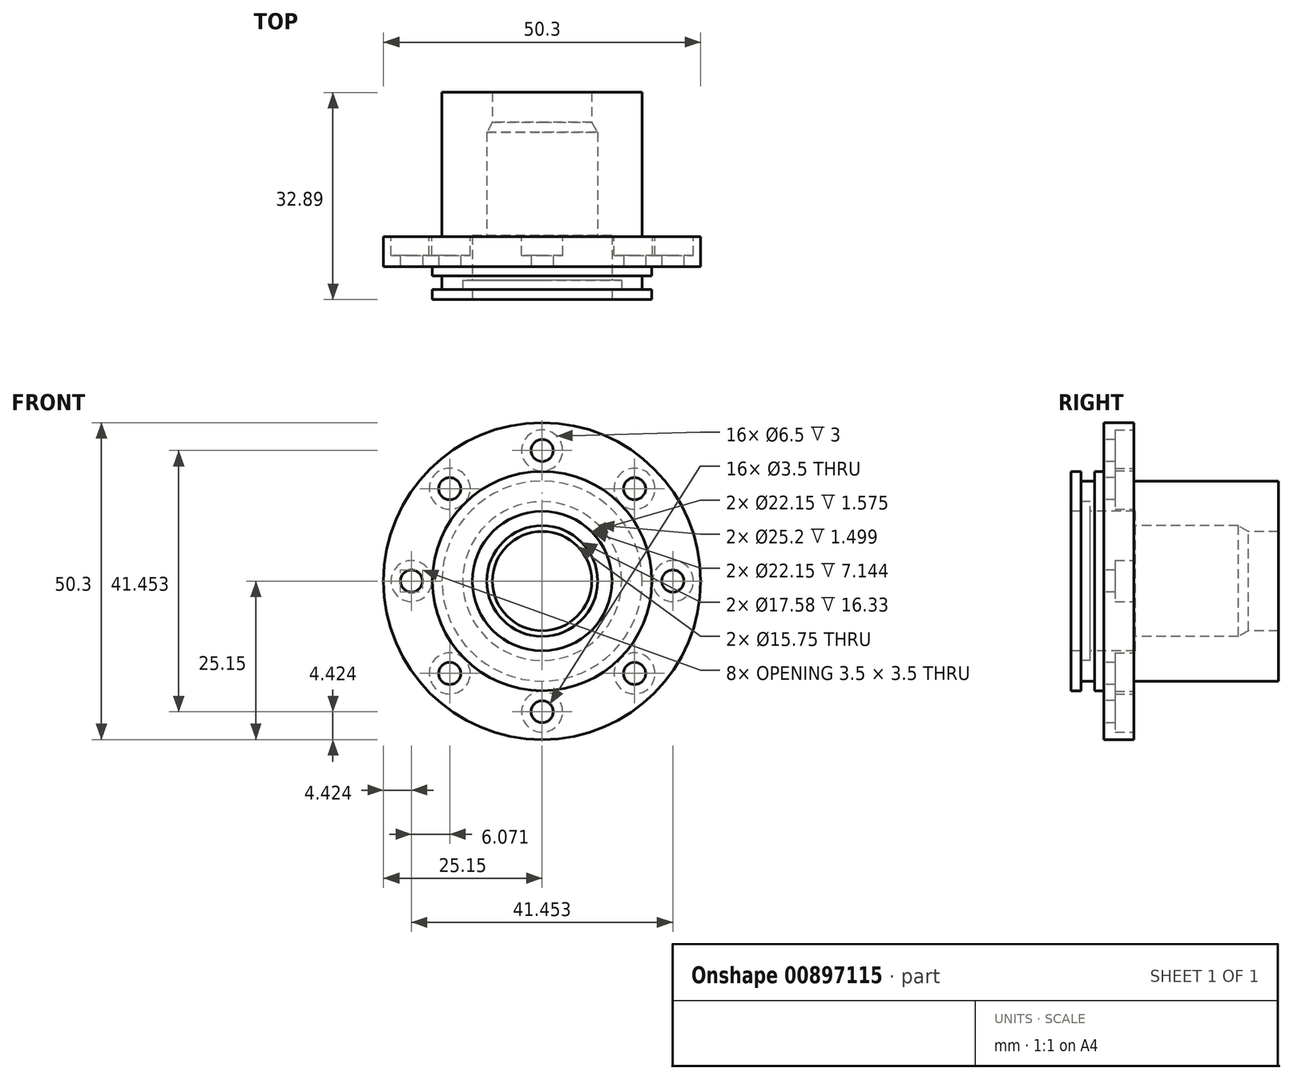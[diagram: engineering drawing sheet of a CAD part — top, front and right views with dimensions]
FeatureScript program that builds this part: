
annotation { "Feature Type Name" : "Feature", "Feature Type Description" : "" }
export const myFeature = defineFeature(function(context is Context, id is Id, definition is map)
    precondition{}
    {
        {
            var Q0;
            Q0=qCreatedBy(makeId("Right.planeOp"),FACE);
            var sketch = newSketch(context, id + "F0", { "sketchPlane" : qUnion([Q0])});
            skLineSegment(sketch, "E0", {"start": v(0, 17.4) * mm, "end": v(1.63, 17.4) * mm});
            skLineSegment(sketch, "E1", {"start": v(1.63, 17.4) * mm, "end": v(1.63, 15.88) * mm});
            skLineSegment(sketch, "E2", {"start": v(5.23, 25.15) * mm, "end": v(10, 25.15) * mm});
            skLineSegment(sketch, "E3", {"start": v(10, 25.15) * mm, "end": v(10, 15.87) * mm});
            skLineSegment(sketch, "E4", {"start": v(10, 15.87) * mm, "end": v(32.9, 15.88) * mm});
            skLineSegment(sketch, "E5", {"start": v(0, 17.4) * mm, "end": v(0, 11.07) * mm});
            skLineSegment(sketch, "E6", {"start": v(0, 11.07) * mm, "end": v(1.57, 11.07) * mm});
            skLineSegment(sketch, "E7", {"start": v(1.57, 11.07) * mm, "end": v(1.57, 12.6) * mm});
            skLineSegment(sketch, "E8", {"start": v(1.57, 12.6) * mm, "end": v(3.07, 12.6) * mm});
            skLineSegment(sketch, "E9", {"start": v(3.07, 12.6) * mm, "end": v(3.07, 11.07) * mm});
            skLineSegment(sketch, "E10", {"start": v(3.07, 11.07) * mm, "end": v(10.22, 11.07) * mm});
            skLineSegment(sketch, "E11", {"start": v(10.22, 11.07) * mm, "end": v(10.22, 8.79) * mm});
            skLineSegment(sketch, "E12", {"start": v(28.13, 7.87) * mm, "end": v(32.9, 7.87) * mm});
            skLineSegment(sketch, "E13", {"start": v(32.9, 7.87) * mm, "end": v(32.9, 15.88) * mm});
            skLineSegment(sketch, "E14", {"start": v(0, 0) * mm, "end": v(32.9, 0) * mm, "construction": true});
            skLineSegment(sketch, "E15", {"start": v(1.63, 15.88) * mm, "end": v(3.76, 15.88) * mm});
            skLineSegment(sketch, "E16", {"start": v(3.76, 15.88) * mm, "end": v(3.76, 17.4) * mm});
            skLineSegment(sketch, "E17", {"start": v(3.76, 17.4) * mm, "end": v(5.23, 17.4) * mm});
            skLineSegment(sketch, "E18", {"start": v(5.23, 17.4) * mm, "end": v(5.23, 25.15) * mm});
            skLineSegment(sketch, "E19", {"start": v(10.22, 8.79) * mm, "end": v(26.55, 8.79) * mm});
            skLineSegment(sketch, "E20", {"start": v(26.55, 8.79) * mm, "end": v(28.13, 7.87) * mm});
            skSolve(sketch);
        }
        {
            var Q0;
            Q0=qSketchRegion(id+"F0",true);
            var Q1;
            Q1=sQuery(id+"F0.wireOp",EDGE,"E14");
            revolve(context, id + "F1", {"entities" : qUnion([Q0]), "axis" : qUnion([Q1]), "revolveType" : RevolveType.FULL});
        }
        {
            var Q0;
            Q0=makeQuery(id+"F1.opRevolve","SWEPT_FACE",FACE,{"disambiguationData":[OSD([sQuery(id+"F0.wireOp",EDGE,"E3")])]});
            var sketch = newSketch(context, id + "F2", { "sketchPlane" : qUnion([Q0])});
            skCircle(sketch, "E21", {"center": v(0, 20.73) * mm, "radius": 3.25 * mm});
            skCircle(sketch, "E22.1.0", {"center": v(-14.66, 14.66) * mm, "radius": 3.25 * mm});
            skCircle(sketch, "E22.2.0", {"center": v(-20.73, 0) * mm, "radius": 3.25 * mm});
            skCircle(sketch, "E22.3.0", {"center": v(-14.66, -14.66) * mm, "radius": 3.25 * mm});
            skCircle(sketch, "E22.4.0", {"center": v(0, -20.73) * mm, "radius": 3.25 * mm});
            skCircle(sketch, "E22.5.0", {"center": v(14.66, -14.66) * mm, "radius": 3.25 * mm});
            skCircle(sketch, "E22.6.0", {"center": v(20.73, 0) * mm, "radius": 3.25 * mm});
            skCircle(sketch, "E22.7.0", {"center": v(14.66, 14.66) * mm, "radius": 3.25 * mm});
            skPoint(sketch, "E22.center", {"position": v(0, 0) * mm});
            skSolve(sketch);
        }
        {
            var Q0;
            Q0=qSketchRegion(id+"F2",true);
            extrude(context, id + "F3", {"entities" : qUnion([Q0]), "operationType" : NewBodyOperationType.REMOVE, "oppositeDirection" : true, "depth" : 3 * mm});
        }
        {
            var Q0;
            Q0=qCreatedBy(makeId("Front.planeOp"),FACE);
            var sketch = newSketch(context, id + "F4", { "sketchPlane" : qUnion([Q0])});
            skCircle(sketch, "E23", {"center": v(0, 20.73) * mm, "radius": 1.75 * mm});
            skCircle(sketch, "E24.1.0", {"center": v(-14.66, 14.66) * mm, "radius": 1.75 * mm});
            skCircle(sketch, "E24.2.0", {"center": v(-20.73, 0) * mm, "radius": 1.75 * mm});
            skCircle(sketch, "E24.3.0", {"center": v(-14.66, -14.66) * mm, "radius": 1.75 * mm});
            skCircle(sketch, "E24.4.0", {"center": v(0, -20.73) * mm, "radius": 1.75 * mm});
            skCircle(sketch, "E24.5.0", {"center": v(14.66, -14.66) * mm, "radius": 1.75 * mm});
            skCircle(sketch, "E24.6.0", {"center": v(20.73, 0) * mm, "radius": 1.75 * mm});
            skCircle(sketch, "E24.7.0", {"center": v(14.66, 14.66) * mm, "radius": 1.75 * mm});
            skPoint(sketch, "E24.center", {"position": v(0, 0) * mm});
            skSolve(sketch);
        }
        {
            var Q0;
            Q0=qSketchRegion(id+"F4",true);
            extrude(context, id + "F5", {"entities" : qUnion([Q0]), "operationType" : NewBodyOperationType.REMOVE, "endBound" : BoundingType.THROUGH_ALL, "oppositeDirection" : true, "depth" : 25.4 * mm});
        }
    });
